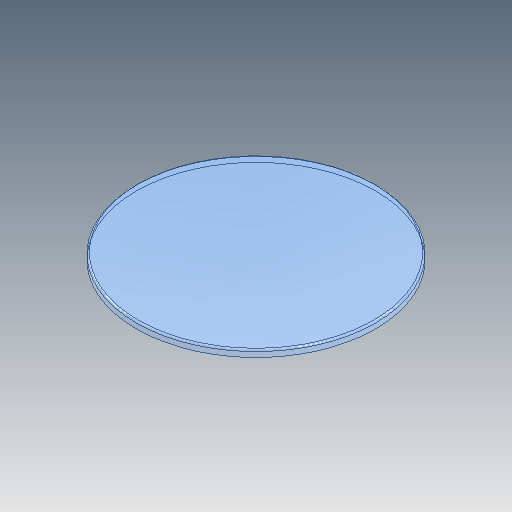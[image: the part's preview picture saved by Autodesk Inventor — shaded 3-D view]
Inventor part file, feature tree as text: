
AUTODESK INVENTOR PART (.ipt)
format: ipt  version: 2020.3 (Build 243373000, 373)  size: 97,280 bytes
history: native  units: mm
features: other x3, sketch x1
ambient origin geometry x8: Origin, YZ Plane, XZ Plane, XY Plane, X Axis, Y Axis, Z Axis, Center Point
bodies: Solid1 (feature_tree)
feature tree (4):
  other  "LensV2.ipt"
  other  "Solid1::LensV2.ipt"
  other  "TaggingFeature1"
  sketch  "Sketch1"  dims[d0=10.0mm]
